# Revit family: Plumbing-Faucet-Sloan-Valve-EFX-300
name_source: partatom
category: Plumbing Fixtures
units: mm (PartAtom-declared; Revit-internal decimal feet)

## family parameters
Cut with Voids When Loaded = No
Host = Face
Maintain Annotation Orientation = No
OmniClass Number = 23.45.55.14
OmniClass Title = Single Faucets
Part Type = Normal
Room Calculation Point = No
Round Connector Dimension = Use Diameter
Shared = No

## types (34) — shared parameters
Apparent Load = 0 VA
Assembly Code = D2010
CW Connection = Yes
CWFU = 1.5
Cold Water Connection Diameter = 0"
Connector Description = Electrical Connection
Current = 0 A
Default Elevation = 0"
Depth = 6"
Edition number = 1
HW Connection = Yes
HWFU = 1.5
Height = 5"
Hot Water Connection Diameter = 0"
Hot Water Connector Description = Hot Water Connection
Keynote = 15410
Manufacturer = Sloan Valve
Number of Poles = 1
Power Factor = 1
Product Material = Sloan Valve - Finish - Polished Chrome
Product data url = https://bimobject.com
URL = www.sloanvalve.com
Valve Pressure Drop = 0.00 psi
Vent Connection = No
Voltage = 120 V
Waste Connection = No
zero-valued in all types: WFU

## per-type parameters (varying)
| type | Battery Powered | Description | Hardwired | Part Number | Water Flow | Width | z_No Trim Plate | z_Trim Plate 4 | z_Trim Plate 8 | z_Trim Plate Length |
| EFX-300-PLG-TEE-CP-1.5GPM-MLM-CAP-BAA-FCT | No | Plug Adapter Power Supply, Back-Check Tee, Polished Chrome Finish, 1.5 gpm, Multi-Laminar Spray, Capacitance Sensor, BASYS® Hardwired-Powered Deck-Mounted Low Body. | Yes | 3324350 | 2 GPM | 2 1/4" | Yes | No | No | 5" |
| EFX-300-PLG-TEE-CP-1.5GPM-IR-FCT | No | Plug Adapter Power Supply, Back-Check Tee, Polished Chrome Finish, 1.5 gpm, Aerated (installed) or Laminar (in box) Spray, Infrared Sensor, BASYS® Hardwired-Powered Deck-Mounted Low Body. | Yes | 3324092 | 2 GPM | 2 1/4" | Yes | No | No | 5" |
| EFX-300-PLG-TEE-CP-1.5GPM-CAP-BAA-FCT | No | Plug Adapter Power Supply, Back-Check Tee, Polished Chrome Finish, 1.5 gpm, Aerated (installed) or Laminar (in box) Spray, Capacitance Sensor, BASYS® Hardwired-Powered Deck-Mounted Low Body. | Yes | 3324269 | 2 GPM | 2 1/4" | Yes | No | No | 5" |
| EFX-300-PLG-TEE-CP-0.5GPM-MLM-IR-FCT | No | Plug Adapter Power Supply, Back-Check Tee, Polished Chrome Finish, 0.5 gpm, Multi-Laminar Spray, Infrared Sensor, BASYS® HardwiredPowered Deck-Mounted Low Body. | Yes | 3324096 | 1 GPM | 2 1/4" | Yes | No | No | 5" |
| EFX-300-PLG-TEE-CP-0.5GPM-MLM-CAP-BAA-FCT | No | Plug Adapter Power Supply, Back-Check Tee, Polished Chrome Finish, 0.5 gpm, Multi-Laminar Spray, Capacitance Sensor, BASYS® Hardwired-Powered Deck-Mounted Low Body. | Yes | 3324007 | 1 GPM | 2 1/4" | Yes | No | No | 5" |
| EFX-300-PLG-ISM-CP-1.5GPM-IR-FCT | No | Plug Adapter Power Supply, Integrated Side Mixer, Polished Chrome Finish, 1.5 gpm, Aerated (installed) or Laminar (in box) Spray, Infrared Sensor, BASYS® Hardwired-Powered Deck-Mounted Low Body. | Yes | 3324295 | 2 GPM | 2 1/4" | Yes | No | No | 5" |
| EFX-300-PLG-ISM-CP-0.5GPM-MLM-IR-FCT | No | Plug Adapter Power Supply, Integrated Side Mixer, Polished Chrome Finish, 0.5 gpm, Multi-Laminar Spray, Infrared Sensor, BASYS® Hardwired-Powered Deck-Mounted Low Body. | Yes | 3324097 | 1 GPM | 2 1/4" | Yes | No | No | 5" |
| EFX-300-PLG-BDT-CP-1.5GPM-IR-FCT | No | Plug Adapter Power Supply, Below Deck Thermostatic Mixing Valve, Polished Chrome Finish, 1.5 gpm, Aerated (installed) or Laminar (in box) Spray, Infrared Sensor, BASYS® Hardwired-Powered DeckMounted Low Body. | Yes | 3324093 | 2 GPM | 2 1/4" | Yes | No | No | 5" |
| EFX-300-PLG-BDT-CP-0.5GPM-MLM-IR-FCT | No | Plug Adapter Power Supply, Below Deck Thermostatic Mixing Valve, Polished Chrome Finish, 0.5 gpm, Multi-Laminar Spray, Infrared Sensor, BASYS® Hardwired-Powered Deck-Mounted Low Body. | Yes | 3324434 | 1 GPM | 2 1/4" | Yes | No | No | 5" |
| EFX-300-PLG-BDM-CP-0.5GPM-MLM-IR-FCT | No | Plug Adapter Power Supply, Below Deck Manual Mixing Valve, Polished Chrome Finish, 0.5 gpm, Multi-Laminar Spray, Infrared Sensor, BASYS® Hardwired-Powered Deck-Mounted Low Body. | Yes | 3324046 | 1 GPM | 2 1/4" | Yes | No | No | 5" |
| EFX-300-PLG-BDM-CP-0.5GPM-MLM-CAP-BAA-FCT | No | Plug Adapter Power Supply, Below Deck Manual Mixing Valve, Polished Chrome Finish, 0.5 gpm, Multi-Laminar Spray, Capacitance Sensor, BASYS® Hardwired-Powered Deck-Mounted Low Body. | Yes | 3324020 | 1 GPM | 2 1/4" | Yes | No | No | 5" |
| EFX-300-HLP-TEE-CP-1.5GPM-IR-FCT | No | Hardwired Less Plug Power Supply, Back-Check Tee, Polished Chrome Finish, 1.5 gpm, Aerated (installed) or Laminar (in box) Spray, Infrared Sensor, BASYS® Hardwired-Powered Deck-Mounted Low Body. | Yes | 3324392 | 2 GPM | 2 1/4" | Yes | No | No | 5" |
| EFX-300-HLP-TEE-CP-0.5GPM-MLM-IR-FCT | No | Hardwired Less Plug Power Supply, Back-Check Tee, Polished Chrome Finish, 0.5 gpm, Multi-Laminar Spray, Infrared Sensor, BASYS® Hardwired-Powered Deck-Mounted Low Body. | Yes | 3324088 | 1 GPM | 2 1/4" | Yes | No | No | 5" |
| EFX-300-HLP-ISM-CP-0.5GPM-MLM-IR-FCT | No | Hardwired Less Plug Power Supply, Integrated Side Mixer, Polished Chrome Finish, 0.5 gpm, Multi-Laminar Spray, Infrared Sensor, BASYS® Hardwired-Powered Deck-Mounted Low Body. | Yes | 3324089 | 1 GPM | 2 1/4" | Yes | No | No | 5" |
| EFX-300-HLP-BDT-CP-1.5GPM-IR-FCT | No | Hardwired Less Plug Power Supply, Below Deck Thermostatic Mixing Valve, Polished Chrome Finish, 1.5 gpm, Aerated (installed) or Laminar (in box) Spray, Infrared Sensor, BASYS® Hardwired-Powered Deck-Mounted Low Body. | Yes | 3324379 | 2 GPM | 2 1/4" | Yes | No | No | 5" |
| EFX-300-HLP-BDT-CP-0.5GPM-MLM-IR-FCT | No | Hardwired Less Plug Power Supply, Below Deck Thermostatic Mixing Valve, Polished Chrome Finish, 0.5 gpm, Multi-Laminar Spray, Infrared Sensor, BASYS® Hardwired-Powered Deck-Mounted Low Body. | Yes | 3324391 | 1 GPM | 2 1/4" | Yes | No | No | 5" |
| EFX-300-BOX-TEE-CP-0.5GPM-MLM-IR-FCT | No | Box Transformer Power Supply, Back-Check Tee, Polished Chrome Finish, 0.5 gpm, Multi-Laminar Spray, Infrared Sensor, BASYS® Hardwired-Powered Deck-Mounted Low Body. | Yes | 3324238 | 1 GPM | 2 1/4" | Yes | No | No | 5" |
| EFX-300-BOX-ISM-CP-1.5GPM-IR-FCT | No | Box Transformer Power Supply, Integrated Side Mixer, Polished Chrome Finish, 1.5 gpm, Aerated (installed) or Laminar (in box) Spray, Infrared Sensor, BASYS® Hardwired-Powered Deck-Mounted Low Body. | Yes | 3324263 | 2 GPM | 2 1/4" | Yes | No | No | 5" |
| EFX-300-BOX-ISM-CP-0.5GPM-MLM-IR-FCT | No | Box Transformer Power Supply, Integrated Side Mixer, Polished Chrome Finish, 0.5 gpm, Multi-Laminar Spray, Infrared Sensor, BASYS® Hardwired-Powered Deck-Mounted Low Body. | Yes | 3324452 | 1 GPM | 2 1/4" | Yes | No | No | 5" |
| EFX-300-BOX-BDT-CP-0.5GPM-MLM-IR-FCT | No | Box Transformer Power Supply, Below Deck Thermostatic Mixing Valve, Polished Chrome Finish, 0.5 gpm, Multi-Laminar Spray, Infrared Sensor, BASYS® Hardwired-Powered Deck-Mounted Low Body. | Yes | 3324329 | 1 GPM | 2 1/4" | Yes | No | No | 5" |
| EFX-300-8-PLG-TEE-CP-0.5GPM-MLM-IR-FCT | No | 8" Trim Plate, Plug Adapter Power Supply, Back-Check Tee, Polished Chrome Finish, 0.5 gpm, Multi-Laminar Spray, Infrared Sensor, BASYS® Hardwired-Powered Deck-Mounted Low Body. | Yes | 3324346 | 1 GPM | 10 1/4" | No | No | Yes | 10 1/4" |
| EFX-300-4-PLG-BDT-CP-0.5GPM-MLM-IR-FCT | No | 4" Trim Plate, Plug Adapter Power Supply, Below Deck Thermostatic Mixing Valve, Polished Chrome Finish, 0.5 gpm, Multi-Laminar Spray, Infrared Sensor, BASYS® Hardwired-Powered Deck-Mounted Low Body. | Yes | 3324382 | 1 GPM | 6 1/8" | No | Yes | No | 6 1/8" |
| EFX-300-4-PLG-BDT-CP-0.5GPM-MLM-CAP-BAA-FCT | No | 4" Trim Plate, Plug Adapter Power Supply, Below Deck Thermostatic Mixing Valve, Polished Chrome Finish, 0.5 gpm, Multi-Laminar Spray, Capacitance Sensor, BASYS® Hardwired-Powered Deck-Mounted Low Body. | Yes | 3324210 | 1 GPM | 6 1/8" | No | Yes | No | 6 1/8" |
| EFX-300-8-PLG-ISM-CP-1.5GPM-IR-FCT | No | 8" Trim Plate, Plug Adapter Power Supply, Integrated Side Mixer, Polished Chrome Finish, 1.5 gpm, Aerated (installed) or Laminar (in box) Spray, Infrared Sensor, BASYS® Hardwired-Powered DeckMounted Low Body. | Yes | 3324330 | 2 GPM | 10 1/4" | No | No | Yes | 10 1/4" |
| EFX-300-BAT-BDM-CP-0.5GPM-MLM-CAP-BAA-FCT | Yes | Battery Power Supply, Below Deck Manual Mixing Valve, Polished Chrome Finish, 0.5 gpm, Multi-Laminar Spray, Capacitance Sensor, BASYS® Hardwired-Powered Deck-Mounted Low Body. | No | 3324383 | 1 GPM | 2 1/4" | Yes | No | No | 5" |
| EFX-300-PLG-TEE-CP-0.35GPM-MLM-IR-FCT | No | Plug Adapter Power Supply, Back-Check Tee, Polished Chrome Finish, 0.35 gpm, Multi-Laminar Spray, Infrared Sensor, BASYS® HardwiredPowered Deck-Mounted Low Body. | Yes | 33243154 | 0 GPM | 2 1/4" | Yes | No | No | 5" |
| EFX-300-PLG-ISM-CP-0.35GPM-MLM-IR-FCT | No | Plug Adapter Power Supply, Integrated Side Mixer, Polished Chrome Finish, 0.35 gpm, Multi-Laminar Spray, Infrared Sensor, BASYS® Hardwired-Powered Deck-Mounted Low Body. | Yes | 33243153 | 0 GPM | 2 1/4" | Yes | No | No | 5" |
| EFX-300-PLG-BDT-CP-0.35GPM-MLM-IR-FCT | No | Plug Adapter Power Supply, Below Deck Thermostatic Mixing Valve, Polished Chrome Finish, 0.35 gpm, Multi-Laminar Spray, Infrared Sensor, BASYS® Hardwired-Powered Deck-Mounted Low Body. | Yes | 33243152 | 0 GPM | 2 1/4" | Yes | No | No | 5" |
| EFX-300-PLG-BDM-CP-0.35GPM-MLM-IR-FCT | No | Plug Adapter Power Supply, Below Deck Manual Mixing Valve, Polished Chrome Finish, 0.35 gpm, Multi-Laminar Spray, Infrared Sensor, BASYS® Hardwired-Powered Deck-Mounted Low Body. | Yes | 33243151 | 0 GPM | 2 1/4" | Yes | No | No | 5" |
| EFX-300-HLP-TEE-CP-0.35GPM-MLM-IR-FCT | No | Hardwired Less Plug Power Supply, Back-Check Tee, Polished Chrome Finish, 0.35 gpm, Multi-Laminar Spray, Infrared Sensor, BASYS® Hardwired-Powered Deck-Mounted Low Body. | Yes | 33243149 | 0 GPM | 2 1/4" | Yes | No | No | 5" |
| EFX-300-HLP-ISM-CP-0.35GPM-MLM-IR-FCT | No | Hardwired Less Plug Power Supply, Integrated Side Mixer, Polished Chrome Finish, 0.35 gpm, Multi-Laminar Spray, Infrared Sensor, BASYS® Hardwired-Powered Deck-Mounted Low Body. | Yes | 33243148 | 0 GPM | 2 1/4" | Yes | No | No | 5" |
| EFX-300-HLP-BDT-CP-0.35GPM-MLM-IR-FCT | No | Hardwired Less Plug Power Supply, Below Deck Thermostatic Mixing Valve, Polished Chrome Finish, 0.35 gpm, Multi-Laminar Spray, Infrared Sensor, BASYS® Hardwired-Powered Deck-Mounted Low Body. | Yes | 33243147 | 0 GPM | 2 1/4" | Yes | No | No | 5" |
| EFX-300-8-PLG-TEE-CP-0.35GPM-MLM-IR-FCT | No | 8" Trim Plate, Plug Adapter Power Supply, Back-Check Tee, Polished Chrome Finish, 0.35 gpm, Multi-Laminar Spray, Infrared Sensor, BASYS® Hardwired-Powered Deck-Mounted Low Body. | Yes | 33243146 | 0 GPM | 10 1/4" | No | No | Yes | 10 1/4" |
| EFX-300-4-PLG-BDT-CP-0.35GPM-MLM-IR-FCT | No | 4" Trim Plate, Plug Adapter Power Supply, Below Deck Thermostatic Mixing Valve, Polished Chrome Finish, 0.35 gpm, Multi-Laminar Spray, Infrared Sensor, BASYS® Hardwired-Powered Deck-Mounted Low Body. | Yes | 33243145 | 0 GPM | 6 1/8" | No | Yes | No | 6 1/8" |

note: column(s) folded — value = type name in every type: Model

## geometry (parser evidence)
native form markers: Sweep x10
no freeform markers — native parametric forms only
